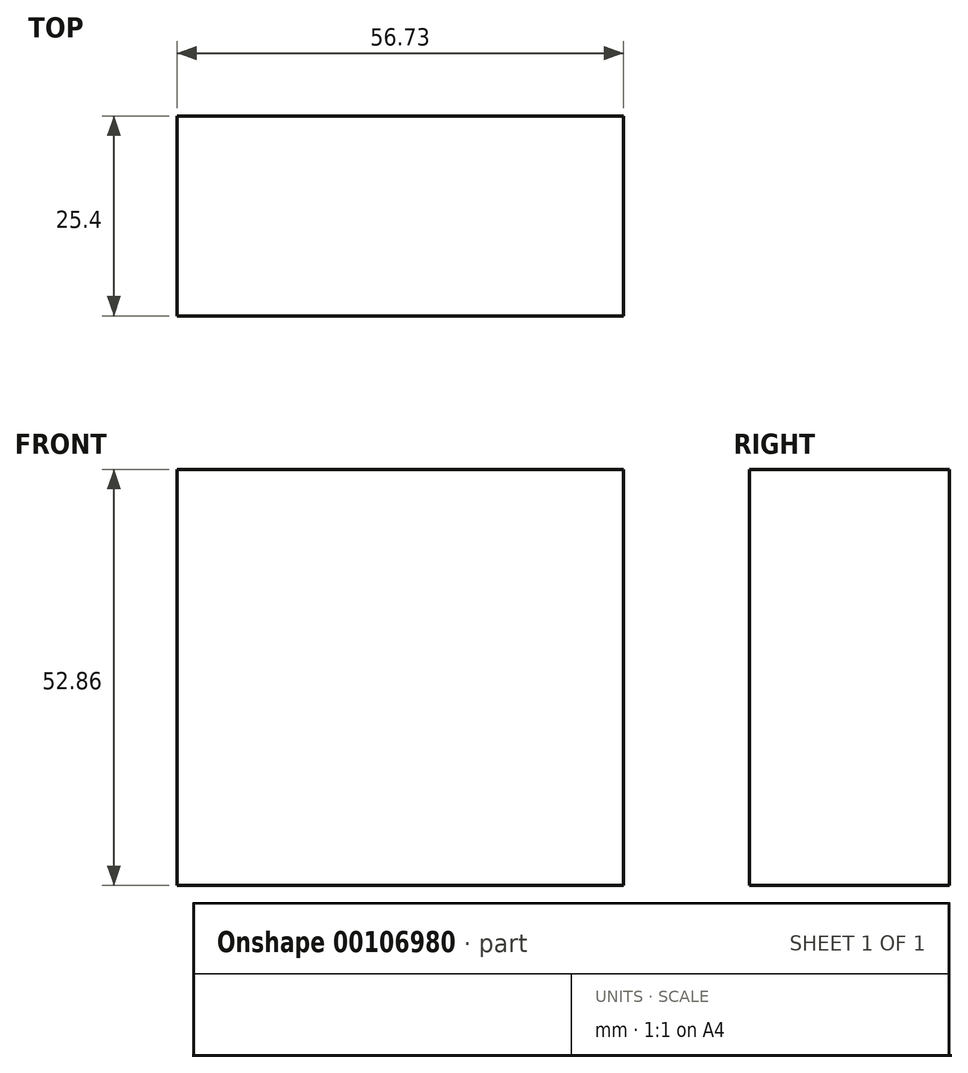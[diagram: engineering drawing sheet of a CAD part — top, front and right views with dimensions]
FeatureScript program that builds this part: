
annotation { "Feature Type Name" : "Feature", "Feature Type Description" : "" }
export const myFeature = defineFeature(function(context is Context, id is Id, definition is map)
    precondition{}
    {
        {
            var Q0;
            Q0=qCreatedBy(makeId("Front.planeOp"),FACE);
            var sketch = newSketch(context, id + "F0", { "sketchPlane" : qUnion([Q0])});
            skLineSegment(sketch, "E0.bottom", {"start": v(0, 0) * mm, "end": v(56.73, 0) * mm});
            skLineSegment(sketch, "E0.top", {"start": v(0, 52.86) * mm, "end": v(56.73, 52.86) * mm});
            skLineSegment(sketch, "E0.left", {"start": v(0, 0) * mm, "end": v(0, 52.86) * mm});
            skLineSegment(sketch, "E0.right", {"start": v(56.73, 0) * mm, "end": v(56.73, 52.86) * mm});
            skSolve(sketch);
        }
        {
            var Q0;
            Q0 = qSketchRegion(id + "F0", true);
            extrude(context, id + "F1", {"entities" : qUnion([Q0]), "depth" : 25.4 * mm});
        }
    });
